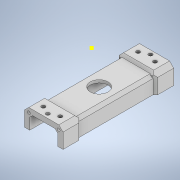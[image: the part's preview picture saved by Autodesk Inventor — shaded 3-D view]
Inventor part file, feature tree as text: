
AUTODESK INVENTOR PART (.ipt)
format: ipt  version: 2022 (Build 260153000, 153)  size: 683,008 bytes
history: native  units: in
note: dims shown in document units (in); Inventor stores cm internally (conversion verified against a paired STEP export)
features: sketch x28, extrude x26, projected_geometry x17, chamfer x7
ambient origin geometry x8: Origin, YZ Plane, XZ Plane, XY Plane, X Axis, Y Axis, Z Axis, Center Point
bodies: Solid1 (feature_tree)
feature tree (78):
  extrude  "Extrusion1"  TaperAngle=75.0deg  [1 undecoded]
  extrude  "Extrusion2"  Depth=0.0787in TaperAngle=0.0deg
  chamfer  "Chamfer1"  Distance=0.1181in
  chamfer  "Chamfer2"  Distance=0.1969in Angle=45.0deg
  chamfer  "Chamfer3"  Distance=0.1181in Angle=45.0deg
  extrude  "Extrusion3"  Depth=0.0787in
  extrude  "Extrusion4"  Depth=0.0787in
  extrude  "Extrusion5"  Depth=0.1969in TaperAngle=0.0deg
  extrude  "Extrusion6"  Depth=0.5906in TaperAngle=0.0deg
  extrude  "Extrusion7"  Depth=2.7559in
  chamfer  "Chamfer4"  Distance=0.0787in
  extrude  "Extrusion8"  Depth=0.5906in
  extrude  "Extrusion16"  Depth=0.5906in
  extrude  "Extrusion17"  Depth=0.5906in
  extrude  "Extrusion18"  Depth=0.5906in TaperAngle=0.0deg
  extrude  "Extrusion19"  Depth=0.0787in TaperAngle=45.0deg
  chamfer  "Chamfer7"  Distance=0.5709in
  chamfer  "Chamfer8"  Distance=1.1417in
  extrude  "Extrusion20"  Depth=0.5906in
  extrude  "Extrusion21"  Depth=0.5906in
  extrude  "Extrusion22"  Depth=0.5906in TaperAngle=0.0deg
  sketch  "Sketch25"  dims[d40=0.7874in]
  extrude  "Extrusion23"  Depth=0.5906in
  extrude  "Extrusion24"  Depth=0.5906in
  sketch  "Sketch28"  dims[d42=0.894in]
  extrude  "Extrusion27"  Depth=0.1181in TaperAngle=0.0deg
  extrude  "Extrusion28"  Depth=0.5906in TaperAngle=0.0deg
  extrude  "Extrusion29"  Depth=0.5906in
  extrude  "Extrusion30"  Depth=0.5906in
  extrude  "Extrusion31"  Depth=0.5906in
  chamfer  "Chamfer9"  Distance=0.5906in
  extrude  "Extrusion32"  Depth=1.1811in
  extrude  "Extrusion33"  Depth=0.1181in
  extrude  "Extrusion34"  Depth=0.5906in TaperAngle=0.0deg
  extrude  "Extrusion35"  Depth=0.5906in TaperAngle=0.0deg
  sketch  "Sketch1"  dims[d0=3.1496in d4=75.0deg]
  sketch  "Sketch2"  dims[d5=0.1575in d6=2.7559in d7=0.0in d8=0.1181in d9=0.0in d10=0.1969in d11=0.0787in d12=45.0deg d13=0.1181in d14=0.0787in d15=45.0deg]
  projected_geometry  "Projected Loop1"
  sketch  "Sketch3"  dims[d16=0.1181in d17=0.0787in d18=45.0deg d19=0.0787in]
  sketch  "Sketch4"  dims[d20=0.0787in d22=0.0787in]
  sketch  "Sketch5"  dims[d23=0.0787in d24=0.1969in d25=0.0in]
  sketch  "Sketch7"  dims[d26=0.0787in d27=0.5906in d28=0.0in]
  sketch  "Sketch8"  dims[d29=1.5748in d30=2.7559in]
  sketch  "Sketch9"  dims[d31=0.7874in]
  sketch  "Sketch17"  dims[d32=0.8858in]
  projected_geometry  "Projected Loop4"
  sketch  "Sketch18"  dims[d33=1.5748in]
  sketch  "Sketch19"  dims[d34=1.7717in]
  sketch  "Sketch20"  dims[d35=1.1811in]
  projected_geometry  "Projected Loop5"
  sketch  "Sketch21"  dims[d36=0.7874in]
  projected_geometry  "Projected Loop6"
  sketch  "Sketch22"  dims[d37=0.0787in]
  projected_geometry  "Projected Loop7"
  sketch  "Sketch23"  dims[d38=0.7874in]
  projected_geometry  "Projected Loop8"
  projected_geometry  "Projected Loop9"
  projected_geometry  "Projected Loop10"
  projected_geometry  "Projected Loop11"
  projected_geometry  "Projected Loop12"
  sketch  "Sketch24"  dims[d39=0.0787in]
  projected_geometry  "Projected Loop13"
  sketch  "Sketch26"  dims[d41=0.9115in]
  projected_geometry  "Projected Loop14"
  sketch  "Sketch37"  dims[d43=0.1181in]
  projected_geometry  "Projected Loop18"
  sketch  "Sketch38"  dims[d44=0.1181in]
  projected_geometry  "Projected Loop19"
  sketch  "Sketch40"  dims[d45=1.5748in]
  projected_geometry  "Projected Loop20"
  sketch  "Sketch42"  dims[d46=0.0in]
  projected_geometry  "Projected Loop21"
  sketch  "Sketch43"  dims[d47=1.0787in]
  projected_geometry  "Projected Loop22"
  sketch  "Sketch46"  dims[d48=1.3386in]
  sketch  "Sketch48"  dims[d49=0.5197in]
  sketch  "Sketch49"  dims[d50=1.0787in]
  sketch  "Sketch50"  dims[d51=0.0in d52=0.0787in d53=0.2756in d54=0.2657in d55=0.5315in d56=0.3543in d57=0.0in d58=0.0394in d59=0.0787in d60=45.0deg d61=0.5709in d62=1.1417in d63=0.1575in d64=0.1575in d65=39.3307in d66=0.0in d106=1.378in d107=1.378in d108=0.1181in d109=0.0in d110=2.874in d111=0.0in d112=0.5906in d113=0.5906in d114=0.5906in d115=0.5906in d116=1.1811in d117=0.1181in d118=2.874in d119=0.0in d120=2.874in d121=0.0in d122=0.1181in d123=0.0787in d124=45.0deg d125=0.1181in d126=0.0787in d127=45.0deg d128=0.7421in d129=0.1181in d130=0.0in d131=0.0787in d132=0.0787in d133=0.0787in d134=0.0787in d135=7.874in d136=0.0in d137=0.3937in d138=0.0in d139=0.8169in d140=0.0in d141=0.8169in d142=0.0in d147=0.0098in d148=0.0in d149=0.0098in d150=0.0in d151=0.0098in d152=0.0in d153=0.0984in d154=0.7874in d155=0.0in d156=0.0984in d157=0.7874in d158=0.0in d159=0.1181in d160=0.0787in d161=45.0deg d162=0.1181in d163=1.5748in d165=360.0deg d167=0.5906in d168=0.0in d170=1.5748in d171=0.1181in d172=360.0deg d173=0.5906in d174=0.0in d175=0.3543in d176=0.1575in d177=0.1575in d178=1.378in d179=0.0in d180=0.0in d181=0.0in]
note: 1 required parameter value undecoded (feature->parameter linkage not recoverable at this tier; creation-order binding heuristic only, values carry confidence <= 0.55)
